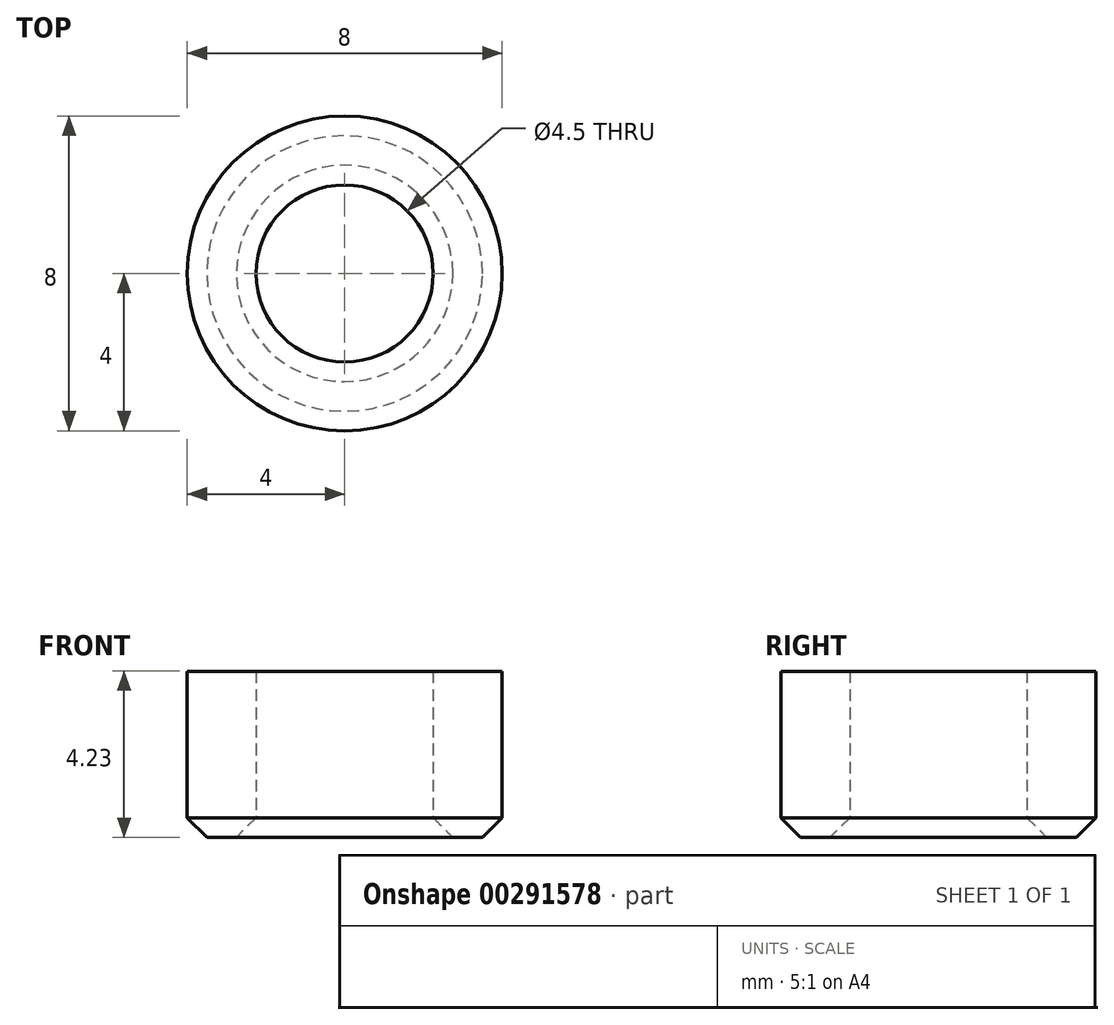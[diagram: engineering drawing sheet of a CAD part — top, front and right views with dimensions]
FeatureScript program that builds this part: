
annotation { "Feature Type Name" : "Feature", "Feature Type Description" : "" }
export const myFeature = defineFeature(function(context is Context, id is Id, definition is map)
    precondition{}
    {
        {
            var Q0;
            Q0=qCreatedBy(makeId("Top.planeOp"),FACE);
            var sketch = newSketch(context, id + "F0", { "sketchPlane" : qUnion([Q0])});
            skCircle(sketch, "E0", {"center": v(0, 0) * mm, "radius": 2.25 * mm});
            skCircle(sketch, "E1", {"center": v(0, 0) * mm, "radius": 4 * mm});
            skSolve(sketch);
        }
        {
            var Q0;
            Q0 = qSketchRegion(id + "F0", true);
            extrude(context, id + "F1", {"entities" : qUnion([Q0]), "depth" : (6 - 2.32 + .546) * mm});
        }
        {
            var Q0;
            Q0=makeQuery(id+"F1.opExtrude","CAP_FACE",FACE,{"disambiguationData":[OSD([sQuery(id+"F0.wireOp",EDGE,"E0"),sQuery(id+"F0.wireOp",EDGE,"E1")])],"isStart":true});
            chamfer(context, id + "F2", {"entities" : qUnion([Q0]), "width" : 0.5 * mm, "tangentPropagation" : true});
        }
    });
